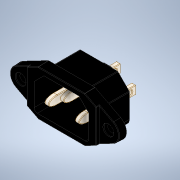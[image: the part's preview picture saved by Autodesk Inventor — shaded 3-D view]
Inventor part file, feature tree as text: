
AUTODESK INVENTOR PART (.ipt)
format: ipt  version: 2020 (Build 240168000, 168)  size: 710,144 bytes
history: mixed  units: in
note: dims shown in document units (in); Inventor stores cm internally (conversion verified against a paired STEP export)
features: other x3, fillet x1, imported_body x1
ambient origin geometry x8: Origin, YZ Plane, XZ Plane, XY Plane, X Axis, Y Axis, Z Axis, Center Point
bodies: Solid1 (imported_parasolid), Solid2 (imported_parasolid), Solid3 (imported_parasolid), Solid4 (imported_parasolid)
feature tree (5):
  other  "Saliente-Extruir3"
  fillet  "Redondeo7"  [1 undecoded]
  other  "Sólido-Mover_Copiar1"
  other  "Sólido-Mover_Copiar2"
  imported_body  NMx_Import_Brep_tag  [imported B-rep: ~14 faces, bbox_mm=None]
note: 1 required parameter value undecoded (feature->parameter linkage not recoverable at this tier; creation-order binding heuristic only, values carry confidence <= 0.55)
